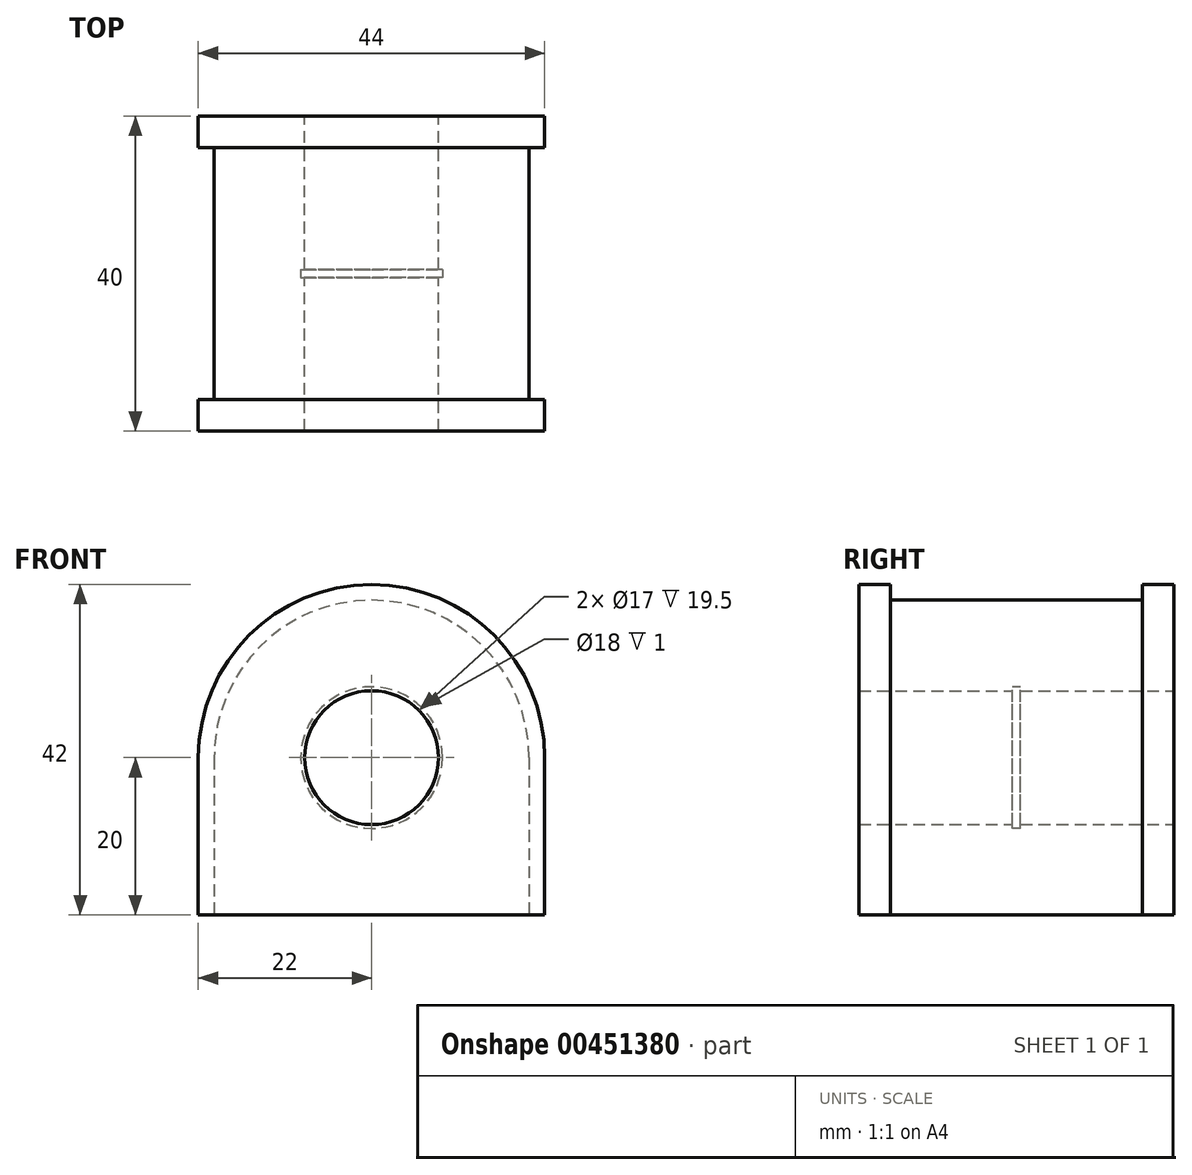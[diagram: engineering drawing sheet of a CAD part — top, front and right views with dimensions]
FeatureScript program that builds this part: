
annotation { "Feature Type Name" : "Feature", "Feature Type Description" : "" }
export const myFeature = defineFeature(function(context is Context, id is Id, definition is map)
    precondition{}
    {
        {
            var Q0;
            Q0=qCreatedBy(makeId("Front.planeOp"),FACE);
            var sketch = newSketch(context, id + "F0", { "sketchPlane" : qUnion([Q0])});
            skCircle(sketch, "E0", {"center": v(0, 0) * mm, "radius": 8.5 * mm});
            skLineSegment(sketch, "E1", {"start": v(-20, 0) * mm, "end": v(-20, -20) * mm});
            skArc(sketch, "E2", {"start": v(20, 0) * mm, "mid": v(0, 20) * mm, "end": v(-20, 0) * mm});
            skLineSegment(sketch, "E3", {"start": v(20, 0) * mm, "end": v(20, -20) * mm});
            skLineSegment(sketch, "E4.0", {"start": v(22, 0) * mm, "end": v(22, -20) * mm});
            skArc(sketch, "E4.1", {"start": v(22, 0) * mm, "mid": v(0, 22) * mm, "end": v(-22, 0) * mm});
            skLineSegment(sketch, "E4.2", {"start": v(-22, 0) * mm, "end": v(-22, -20) * mm});
            skLineSegment(sketch, "E5", {"start": v(-22, -20) * mm, "end": v(22, -20) * mm});
            skLineSegment(sketch, "E6", {"start": v(22, 0) * mm, "end": v(8.5, 0) * mm});
            skCircle(sketch, "E7", {"center": v(0, 0) * mm, "radius": 9 * mm});
            skSolve(sketch);
        }
        {
            var Q0;
            Q0 = qSketchRegion(id + "F0", true);
            var Q1;
            Q1=makeQuery(id+"F0.imprint","IMPRINT",FACE,{"disambiguationData":[TD([[makeQuery(id+"F0.imprint","IMPRINT",EDGE,{"derivedFrom":sQuery(id+"F0.wireOp",EDGE,"E0")}),-1.0]])]});
            extrude(context, id + "F1", {"entities" : qUnion([Q0, Q1]), "endBound" : BoundingType.SYMMETRIC, "depth" : 40 * mm});
        }
        {
            var Q0;
            Q0=makeQuery(id+"F0.imprint","IMPRINT",FACE,{"disambiguationData":[TD([[makeQuery(id+"F0.imprint","IMPRINT",EDGE,{"derivedFrom":sQuery(id+"F0.wireOp",EDGE,"E0")}),-1.0]])]});
            extrude(context, id + "F2", {"entities" : qUnion([Q0]), "operationType" : NewBodyOperationType.REMOVE, "endBound" : BoundingType.SYMMETRIC, "oppositeDirection" : true, "depth" : 1 * mm});
        }
        {
            var Q0;
            {var subQ3=sQuery(id+"F0.wireOp",EDGE,"E1");Q0=makeQuery(id+"F0.imprint","IMPRINT",FACE,{"disambiguationData":[TD([[makeQuery(id+"F0.imprint","IMPRINT",EDGE,{"derivedFrom":subQ3}),-1.0]])]});}
            var Q1;
            {var subQ0=sQuery(id+"F0.wireOp",EDGE,"E3");Q1=makeQuery(id+"F0.imprint","IMPRINT",FACE,{"disambiguationData":[TD([[makeQuery(id+"F0.imprint","IMPRINT",EDGE,{"derivedFrom":subQ0}),1.0]])]});}
            extrude(context, id + "F3", {"entities" : qUnion([Q0, Q1]), "operationType" : NewBodyOperationType.REMOVE, "endBound" : BoundingType.SYMMETRIC, "oppositeDirection" : true, "depth" : 32 * mm});
        }
    });
